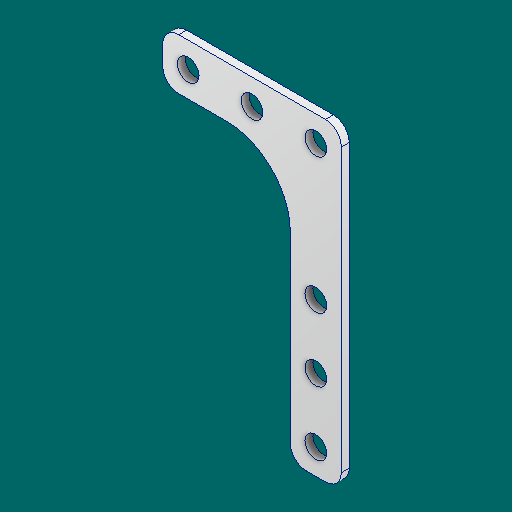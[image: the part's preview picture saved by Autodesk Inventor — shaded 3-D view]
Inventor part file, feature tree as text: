
AUTODESK INVENTOR PART (.ipt)
format: ipt  version: 2023.1 (Build 271208000, 208)  size: 124,928 bytes
history: native  units: in
note: dims shown in document units (in); Inventor stores cm internally (conversion verified against a paired STEP export)
features: other x3, sketch x1
ambient origin geometry x8: Origin, YZ Plane, XZ Plane, XY Plane, X Axis, Y Axis, Z Axis, Center Point
bodies: Solid1 (feature_tree)
feature tree (4):
  other  "Inner_Strut_Gusset.ipt"
  other  "Solid1::Inner_Strut_Gusset.ipt"
  other  "TaggingFeature1"
  sketch  "Sketch1"  dims[d0=0.3937in]
